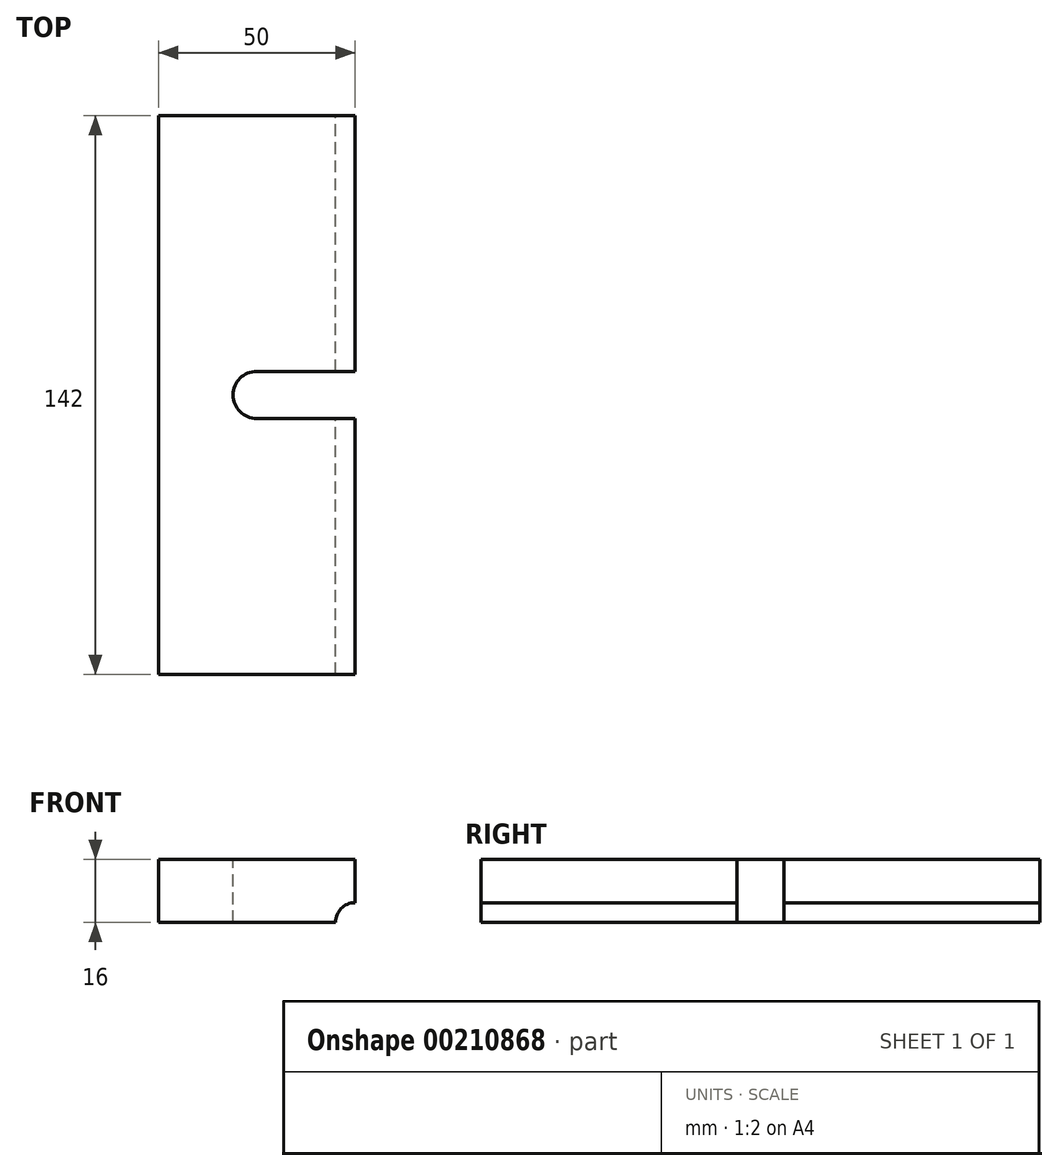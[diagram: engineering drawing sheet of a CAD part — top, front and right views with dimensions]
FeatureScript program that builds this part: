
annotation { "Feature Type Name" : "Feature", "Feature Type Description" : "" }
export const myFeature = defineFeature(function(context is Context, id is Id, definition is map)
    precondition{}
    {
        {
            var Q0;
            Q0=qCreatedBy(makeId("Front.planeOp"),FACE);
            var sketch = newSketch(context, id + "F0", { "sketchPlane" : qUnion([Q0])});
            skLineSegment(sketch, "E0.bottom", {"start": v(25, 8) * mm, "end": v(-25, 8) * mm});
            skLineSegment(sketch, "E0.top", {"start": v(20, -8) * mm, "end": v(-25, -8) * mm});
            skLineSegment(sketch, "E0.left", {"start": v(25, 8) * mm, "end": v(25, -3) * mm});
            skLineSegment(sketch, "E0.right", {"start": v(-25, 8) * mm, "end": v(-25, -8) * mm});
            skPoint(sketch, "E0.middle", {"position": v(0, 0) * mm});
            skArc(sketch, "E1", {"start": v(25, -3) * mm, "mid": v(21.46, -4.46) * mm, "end": v(20, -8) * mm});
            skSolve(sketch);
        }
        {
            var Q0;
            Q0=makeQuery(id+"F0.imprint","IMPRINT",FACE,{"disambiguationData":[TD([[makeQuery(id+"F0.imprint","IMPRINT",EDGE,{"derivedFrom":sQuery(id+"F0.wireOp",EDGE,"E0.bottom")}),1.0]])]});
            extrude(context, id + "F1", {"entities" : qUnion([Q0]), "endBound" : BoundingType.SYMMETRIC, "depth" : 142 * mm});
        }
        {
            var Q0;
            Q0=makeQuery(id+"F1.opExtrude","SWEPT_FACE",FACE,{"disambiguationData":[OSD([sQuery(id+"F0.wireOp",EDGE,"E0.bottom")])]});
            var sketch = newSketch(context, id + "F2", { "sketchPlane" : qUnion([Q0])});
            skCircle(sketch, "E2", {"center": v(0, 0) * mm, "radius": 6 * mm});
            skLineSegment(sketch, "E3", {"start": v(0, 6) * mm, "end": v(25, 6) * mm});
            skLineSegment(sketch, "E4", {"start": v(25, 6) * mm, "end": v(25, -6) * mm});
            skLineSegment(sketch, "E5", {"start": v(25, -6) * mm, "end": v(0, -6) * mm});
            skSolve(sketch);
        }
        {
            var Q0;
            {var subQ0=sQuery(id+"F2.wireOp",EDGE,"E2");var subQ1=makeQuery(id+"F2.imprint","INTERSECT",VERTEX,{"derivedFrom":[subQ0,sQuery(id+"F2.wireOp",EDGE,"E3")]});Q0=makeQuery(id+"F2.imprint","IMPRINT",FACE,{"disambiguationData":[TD([[makeQuery(id+"F2.imprint","IMPRINT",EDGE,{"disambiguationData":[TD([[subQ1,-1.0]])],"derivedFrom":subQ0}),1.0]])]});}
            extrude(context, id + "F3", {"entities" : qUnion([Q0]), "operationType" : NewBodyOperationType.REMOVE, "oppositeDirection" : true, "depth" : 16 * mm});
        }
        {
            var Q0;
            {var subQ0=sQuery(id+"F2.wireOp",EDGE,"E3");Q0=makeQuery(id+"F2.imprint","IMPRINT",FACE,{"disambiguationData":[TD([[makeQuery(id+"F2.imprint","IMPRINT",EDGE,{"derivedFrom":subQ0}),-1.0]])]});}
            extrude(context, id + "F4", {"entities" : qUnion([Q0]), "operationType" : NewBodyOperationType.REMOVE, "oppositeDirection" : true, "depth" : 6 * mm});
        }
        {
            var Q0;
            Q0=makeQuery(id+"F1.opExtrude","SWEPT_FACE",FACE,{"disambiguationData":[OSD([sQuery(id+"F0.wireOp",EDGE,"E0.top")])]});
            var sketch = newSketch(context, id + "F5", { "sketchPlane" : qUnion([Q0])});
            skLineSegment(sketch, "E6.bottom", {"start": v(25.04, 6) * mm, "end": v(0, 6) * mm});
            skLineSegment(sketch, "E6.top", {"start": v(25.04, -6) * mm, "end": v(0, -6) * mm});
            skLineSegment(sketch, "E6.left", {"start": v(25.04, 6) * mm, "end": v(25.04, -6) * mm});
            skLineSegment(sketch, "E6.right", {"start": v(0, 6) * mm, "end": v(0, -6) * mm});
            skPoint(sketch, "E6.middle", {"position": v(12.52, 0) * mm});
            skSolve(sketch);
        }
        {
            var Q0;
            Q0 = qSketchRegion(id + "F5", true);
            extrude(context, id + "F6", {"entities" : qUnion([Q0]), "operationType" : NewBodyOperationType.REMOVE, "oppositeDirection" : true, "depth" : 12.4 * mm});
        }
    });
